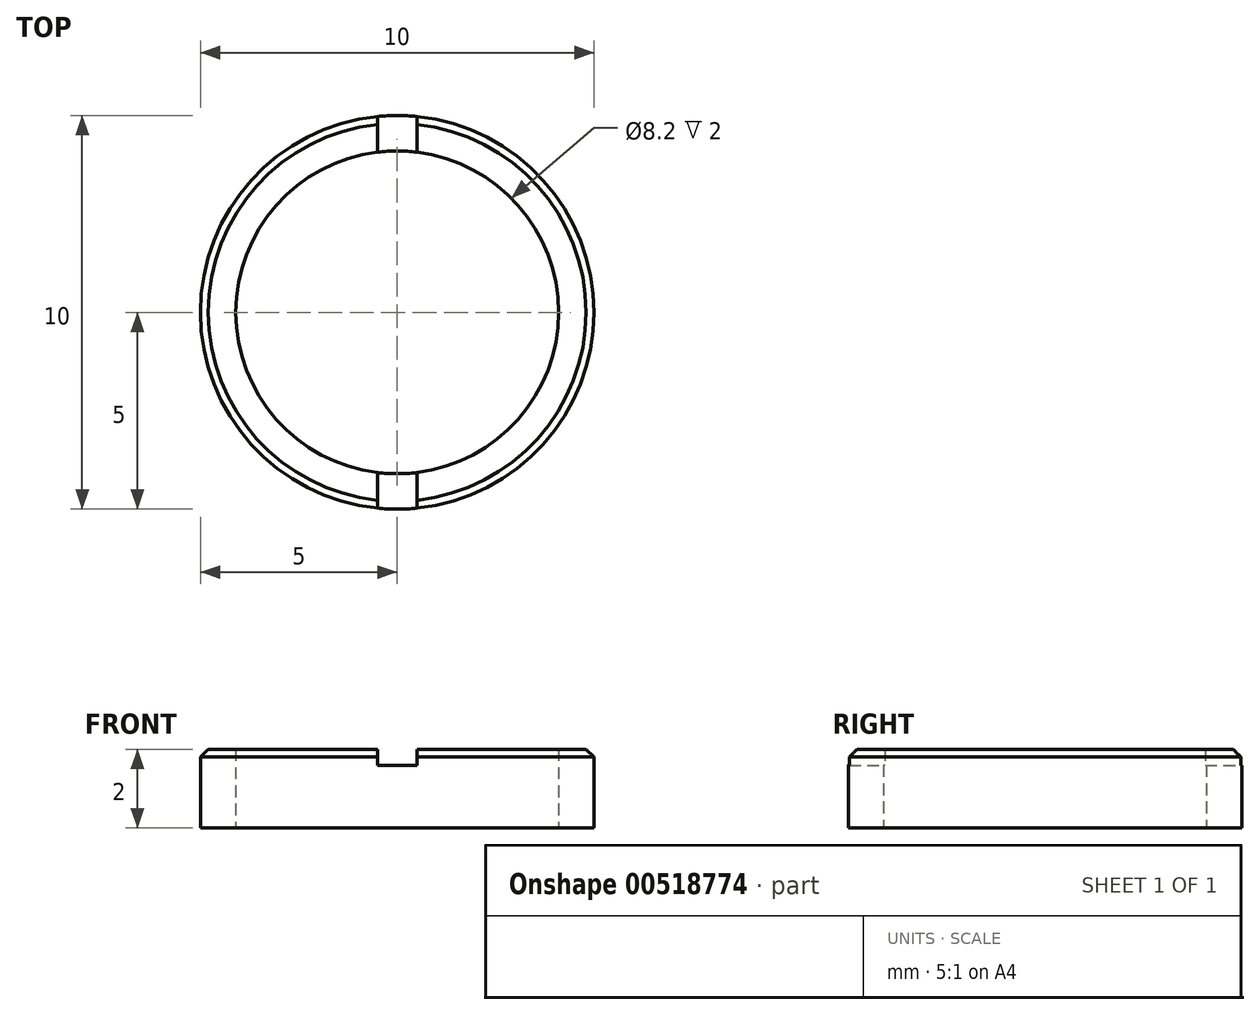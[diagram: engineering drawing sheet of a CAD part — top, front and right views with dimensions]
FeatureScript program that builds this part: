
annotation { "Feature Type Name" : "Feature", "Feature Type Description" : "" }
export const myFeature = defineFeature(function(context is Context, id is Id, definition is map)
    precondition{}
    {
        {
            var Q0;
            Q0=qCreatedBy(makeId("Top.planeOp"),FACE);
            var sketch = newSketch(context, id + "F0", { "sketchPlane" : qUnion([Q0])});
            skCircle(sketch, "E0", {"center": v(0, 0) * mm, "radius": 4.1 * mm});
            skCircle(sketch, "E1", {"center": v(0, 0) * mm, "radius": 5 * mm});
            skSolve(sketch);
        }
        {
            var Q0;
            Q0=qSketchRegion(id+"F0",true);
            extrude(context, id + "F1", {"entities" : qUnion([Q0]), "depth" : 2 * mm, "offsetDistance" : 25 * mm});
        }
        {
            var Q0;
            Q0=makeQuery(id+"F1.opExtrude","CAP_EDGE",EDGE,{"disambiguationData":[OSD([sQuery(id+"F0.wireOp",EDGE,"E1")])],"isStart":false});
            chamfer(context, id + "F2", {"entities" : qUnion([Q0]), "width" : 0.2 * mm, "tangentPropagation" : true});
        }
        {
            var Q0;
            Q0=qCreatedBy(makeId("Front.planeOp"),FACE);
            var sketch = newSketch(context, id + "F3", { "sketchPlane" : qUnion([Q0])});
            skLineSegment(sketch, "E2", {"start": v(0, 2.1) * mm, "end": v(0, 1.6) * mm});
            skLineSegment(sketch, "E3", {"start": v(0, 1.6) * mm, "end": v(1, 1.6) * mm});
            skLineSegment(sketch, "E4", {"start": v(1, 1.6) * mm, "end": v(1, 2.1) * mm});
            skLineSegment(sketch, "E5", {"start": v(1, 2.1) * mm, "end": v(0, 2.1) * mm});
            skSolve(sketch);
        }
        {
            var Q0;
            Q0=qSketchRegion(id+"F3",true);
            extrude(context, id + "F4", {"entities" : qUnion([Q0]), "depth" : 25 * mm, "offsetDistance" : 25 * mm});
        }
        {
            var Q0;
            Q0=makeQuery(id+"F4.opExtrude","SWEPT_BODY",BODY,{"disambiguationData":[OSD([sQuery(id+"F3.wireOp",EDGE,"E2"),sQuery(id+"F3.wireOp",EDGE,"E3"),sQuery(id+"F3.wireOp",EDGE,"E4"),sQuery(id+"F3.wireOp",EDGE,"E5")])]});
            transform(context, id + "F5", {"entities" : qUnion([Q0]), "transformType" : TransformType.TRANSLATION_3D, "dx" : -0.5 * mm, "dy" : 13.3 * mm, "dz" : 0 * mm, "makeCopy" : false});
        }
        {
            var Q0;
            Q0=makeQuery(id+"F4.opExtrude","SWEPT_BODY",BODY,{"disambiguationData":[OSD([sQuery(id+"F3.wireOp",EDGE,"E2"),sQuery(id+"F3.wireOp",EDGE,"E3"),sQuery(id+"F3.wireOp",EDGE,"E4"),sQuery(id+"F3.wireOp",EDGE,"E5")])]});
            var Q1;
            Q1=makeQuery(id+"F1.opExtrude","SWEPT_BODY",BODY,{"disambiguationData":[OSD([sQuery(id+"F0.wireOp",EDGE,"E0"),sQuery(id+"F0.wireOp",EDGE,"E1")])]});
            booleanBodies(context, id + "F6", {"operationType" : BooleanOperationType.SUBTRACTION, "tools" : qUnion([Q0]), "targets" : qUnion([Q1])});
        }
    });
